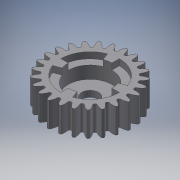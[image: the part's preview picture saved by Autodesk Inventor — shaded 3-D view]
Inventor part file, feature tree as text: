
AUTODESK INVENTOR PART (.ipt)
format: ipt  version: 2017 (Build 210142000, 142)  size: 281,088 bytes
history: native  units: mm
features: extrude x5, sketch x4, pattern_circular x2
ambient origin geometry x8: Origin, YZ Plane, XZ Plane, XY Plane, X Axis, Y Axis, Z Axis, Center Point
bodies: Solid1 (feature_tree)
feature tree (11):
  sketch  "Sketch1"  dims[d0=20.0mm d1=0.0mm]
  extrude  "Extrusion1"  TaperAngle=0.0deg  [1 undecoded]
  extrude  "Extrusion2"  Depth=10.0mm TaperAngle=360.0deg
  pattern_circular  "Circular Pattern1"  [2 undecoded]
  extrude  "Extrusion3"  Depth=15.0mm TaperAngle=0.0deg
  extrude  "Extrusion4"  Depth=5.0mm
  extrude  "Extrusion5"  Depth=5.0mm
  pattern_circular  "Circular Pattern2"  [2 undecoded]
  sketch  "Sketch2"  dims[d2=10.0mm d3=0.0mm d4=250.0mm d5=360.0deg]
  sketch  "Sketch3"  dims[d7=13.5mm]
  sketch  "Sketch4"  dims[d8=10.0mm d9=0.0mm d10=35.0mm d11=15.0mm d12=0.0mm d13=6.0mm d14=12.217305mm d15=5.0mm d16=0.0mm d17=40.0mm d18=360.0deg]
note: 5 required parameter values undecoded (feature->parameter linkage not recoverable at this tier; creation-order binding heuristic only, values carry confidence <= 0.55)
